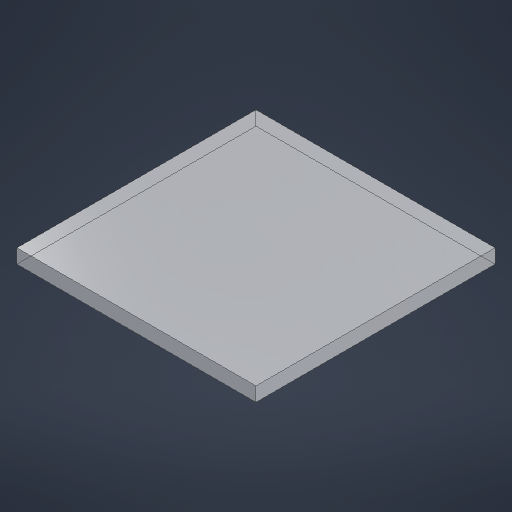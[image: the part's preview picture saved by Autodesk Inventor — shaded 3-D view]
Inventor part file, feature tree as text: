
AUTODESK INVENTOR PART (.ipt)
format: ipt  version: 2025.1 (Build 291241000, 241)  size: 187,392 bytes
history: native  units: mm
features: extrude x1, sketch x1
ambient origin geometry x8: Origin, YZ Plane, XZ Plane, XY Plane, X Axis, Y Axis, Z Axis, Center Point
bodies: Solid1 (feature_tree)
feature tree (2):
  extrude  "Extrusion1"  Depth=25.4mm
  sketch  "Sketch1"  dims[d0=25.4mm d1=25.4mm d2=1.5mm d3=0.0mm]
